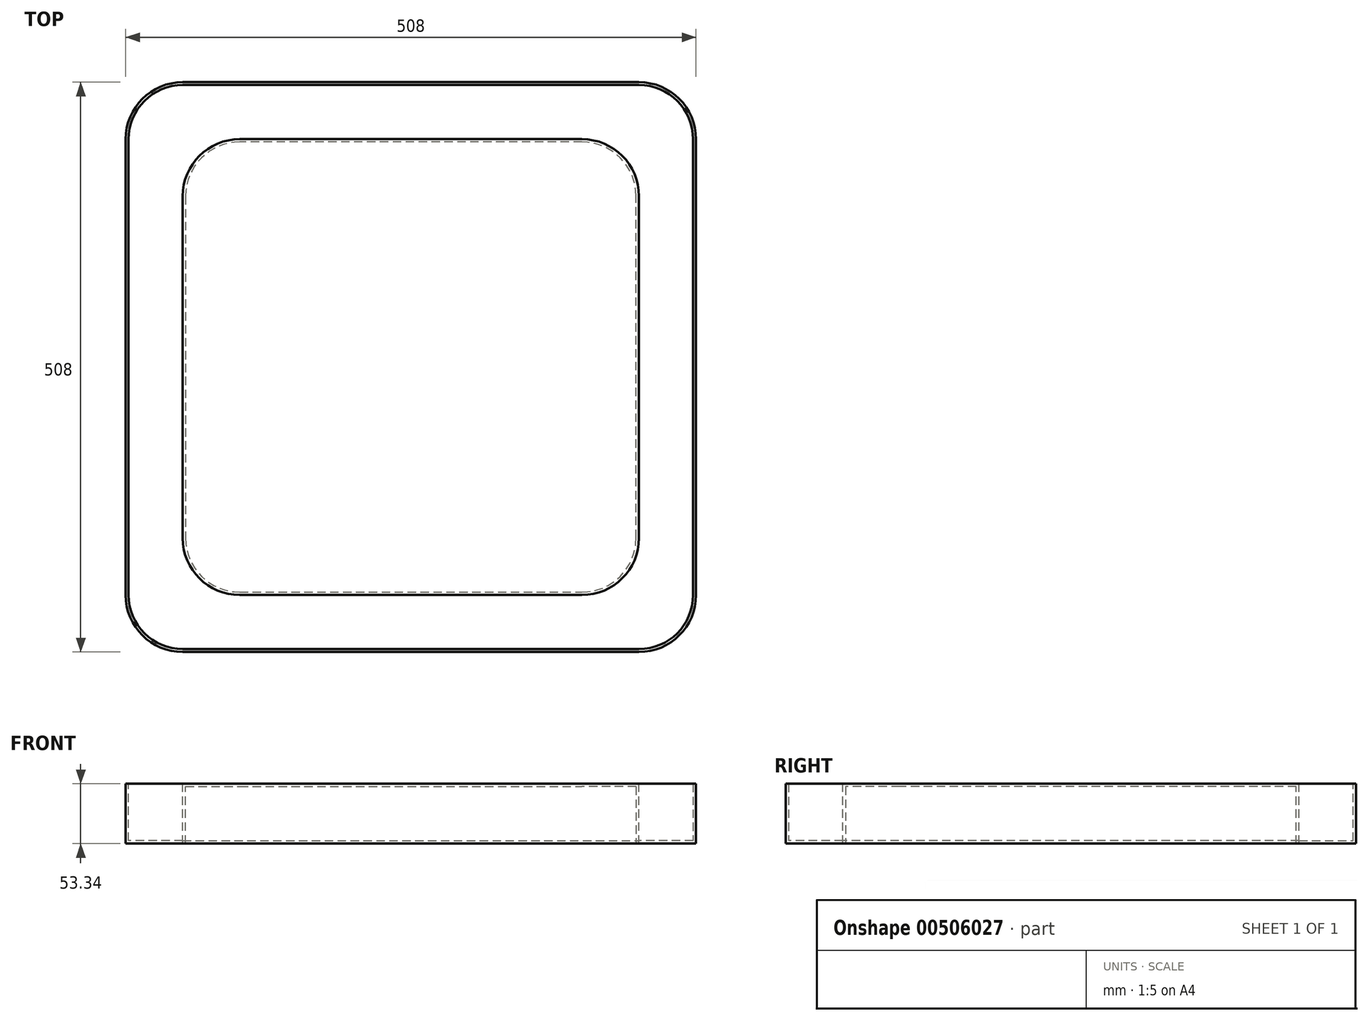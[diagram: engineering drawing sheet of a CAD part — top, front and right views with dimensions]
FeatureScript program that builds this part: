
annotation { "Feature Type Name" : "Feature", "Feature Type Description" : "" }
export const myFeature = defineFeature(function(context is Context, id is Id, definition is map)
    precondition{}
    {
        {
            var Q0;
            Q0=qCreatedBy(makeId("Top.planeOp"),FACE);
            var sketch = newSketch(context, id + "F0", { "sketchPlane" : qUnion([Q0])});
            skLineSegment(sketch, "E0.bottom", {"start": v(50.8, -44.45) * mm, "end": v(457.2, -44.45) * mm});
            skLineSegment(sketch, "E0.top", {"start": v(50.8, 463.55) * mm, "end": v(457.2, 463.55) * mm});
            skLineSegment(sketch, "E0.left", {"start": v(0, 6.35) * mm, "end": v(0, 412.75) * mm});
            skLineSegment(sketch, "E0.right", {"start": v(508, 6.35) * mm, "end": v(508, 412.75) * mm});
            skArc(sketch, "E1", {"start": v(50.8, 463.55) * mm, "mid": v(14.88, 448.67) * mm, "end": v(0, 412.75) * mm});
            skArc(sketch, "E2", {"start": v(508, 412.75) * mm, "mid": v(493.12, 448.67) * mm, "end": v(457.2, 463.55) * mm});
            skArc(sketch, "E3", {"start": v(457.2, -44.45) * mm, "mid": v(493.12, -29.57) * mm, "end": v(508, 6.35) * mm});
            skPoint(sketch, "E4.visualSharp", {"position": v(0, -44.45) * mm});
            skArc(sketch, "E4.filletArc", {"start": v(0, 6.35) * mm, "mid": v(14.88, -29.57) * mm, "end": v(50.8, -44.45) * mm});
            skSolve(sketch);
        }
        {
            var Q0;
            Q0=qCreatedBy(makeId("Top.planeOp"),FACE);
            cPlane(context, id + "F1", {"entities" : qUnion([Q0]), "cplaneType" : CPlaneType.OFFSET, "offset" : 50.8 * mm, "oppositeDirection" : true, "width" : 152.4 * mm, "height" : 152.4 * mm});
        }
        {
            var Q0;
            Q0=qCreatedBy(id+"F1.planeOp",FACE);
            var sketch = newSketch(context, id + "F2", { "sketchPlane" : qUnion([Q0])});
            skLineSegment(sketch, "E5.bottom", {"start": v(101.6, 6.35) * mm, "end": v(406.4, 6.35) * mm});
            skLineSegment(sketch, "E5.top", {"start": v(101.6, 412.75) * mm, "end": v(406.4, 412.75) * mm});
            skLineSegment(sketch, "E5.left", {"start": v(50.8, 57.15) * mm, "end": v(50.8, 361.95) * mm});
            skLineSegment(sketch, "E5.right", {"start": v(457.2, 57.15) * mm, "end": v(457.2, 361.95) * mm});
            skArc(sketch, "E6", {"start": v(101.6, 412.75) * mm, "mid": v(65.68, 397.87) * mm, "end": v(50.8, 361.95) * mm});
            skArc(sketch, "E7", {"start": v(457.2, 361.95) * mm, "mid": v(442.32, 397.87) * mm, "end": v(406.4, 412.75) * mm});
            skArc(sketch, "E8", {"start": v(406.4, 6.35) * mm, "mid": v(442.32, 21.23) * mm, "end": v(457.2, 57.15) * mm});
            skPoint(sketch, "E9.visualSharp", {"position": v(50.8, 6.35) * mm});
            skArc(sketch, "E9.filletArc", {"start": v(50.8, 57.15) * mm, "mid": v(65.68, 21.23) * mm, "end": v(101.6, 6.35) * mm});
            skSolve(sketch);
        }
        {
            var Q0;
            Q0=qCreatedBy(makeId("Right.planeOp"),FACE);
            var sketch = newSketch(context, id + "F3", { "sketchPlane" : qUnion([Q0])});
            skLineSegment(sketch, "E10", {"start": v(0, -53.34) * mm, "end": v(0, 0) * mm});
            skSolve(sketch);
        }
        {
            var Q0;
            Q0 = qSketchRegion(id + "F0", true);
            var Q1;
            Q1 = qSketchRegion(id + "F2", true);
            var Q2;
            Q2 = qSketchRegion(id + "F3", true);
            var Q3;
            Q3 = qConstructionFilter(qBodyType(qCreatedBy(id + "F0" ,EDGE), BodyType.WIRE), ConstructionObject.NO);
            var Q4;
            Q4 = qConstructionFilter(qBodyType(qCreatedBy(id + "F3" ,EDGE), BodyType.WIRE), ConstructionObject.NO);
            sweep(context, id + "F4", {"profiles" : qUnion([Q0, Q1, Q2]), "surfaceProfiles" : qUnion([Q3]), "path" : qUnion([Q4])});
        }
        {
            var Q0;
            Q0=makeQuery(id+"F4.opSweep","CAP_FACE",FACE,{"disambiguationData":[OSD([sQuery(id+"F0.wireOp",EDGE,"E0.bottom"),sQuery(id+"F0.wireOp",EDGE,"E0.top"),sQuery(id+"F0.wireOp",EDGE,"E0.left"),sQuery(id+"F0.wireOp",EDGE,"E0.right"),sQuery(id+"F0.wireOp",EDGE,"E1"),sQuery(id+"F0.wireOp",EDGE,"E2"),sQuery(id+"F0.wireOp",EDGE,"E3"),sQuery(id+"F0.wireOp",EDGE,"E4.filletArc"),sQuery(id+"F3.wireOp",VERTEX,"E10.start")])],"isStart":true});
            shell(context, id + "F5", {"entities" : qUnion([Q0]), "thickness" : 2.54 * mm});
        }
        {
            var Q0;
            Q0=makeQuery(id+"F4.opSweep","CAP_FACE",FACE,{"disambiguationData":[OSD([sQuery(id+"F2.wireOp",EDGE,"E5.bottom"),sQuery(id+"F2.wireOp",EDGE,"E5.top"),sQuery(id+"F2.wireOp",EDGE,"E5.left"),sQuery(id+"F2.wireOp",EDGE,"E5.right"),sQuery(id+"F2.wireOp",EDGE,"E6"),sQuery(id+"F2.wireOp",EDGE,"E7"),sQuery(id+"F2.wireOp",EDGE,"E8"),sQuery(id+"F2.wireOp",EDGE,"E9.filletArc"),sQuery(id+"F3.wireOp",VERTEX,"E10.start")])],"isStart":true});
            shell(context, id + "F6", {"entities" : qUnion([Q0]), "thickness" : 2.54 * mm});
        }
        {
            var Q0;
            Q0=qCreatedBy(makeId("Front.planeOp"),FACE);
            var sketch = newSketch(context, id + "F7", { "sketchPlane" : qUnion([Q0])});
            skLineSegment(sketch, "E11", {"start": v(0, 0) * mm, "end": v(-50.8, 0) * mm});
            skSolve(sketch);
        }
    });
